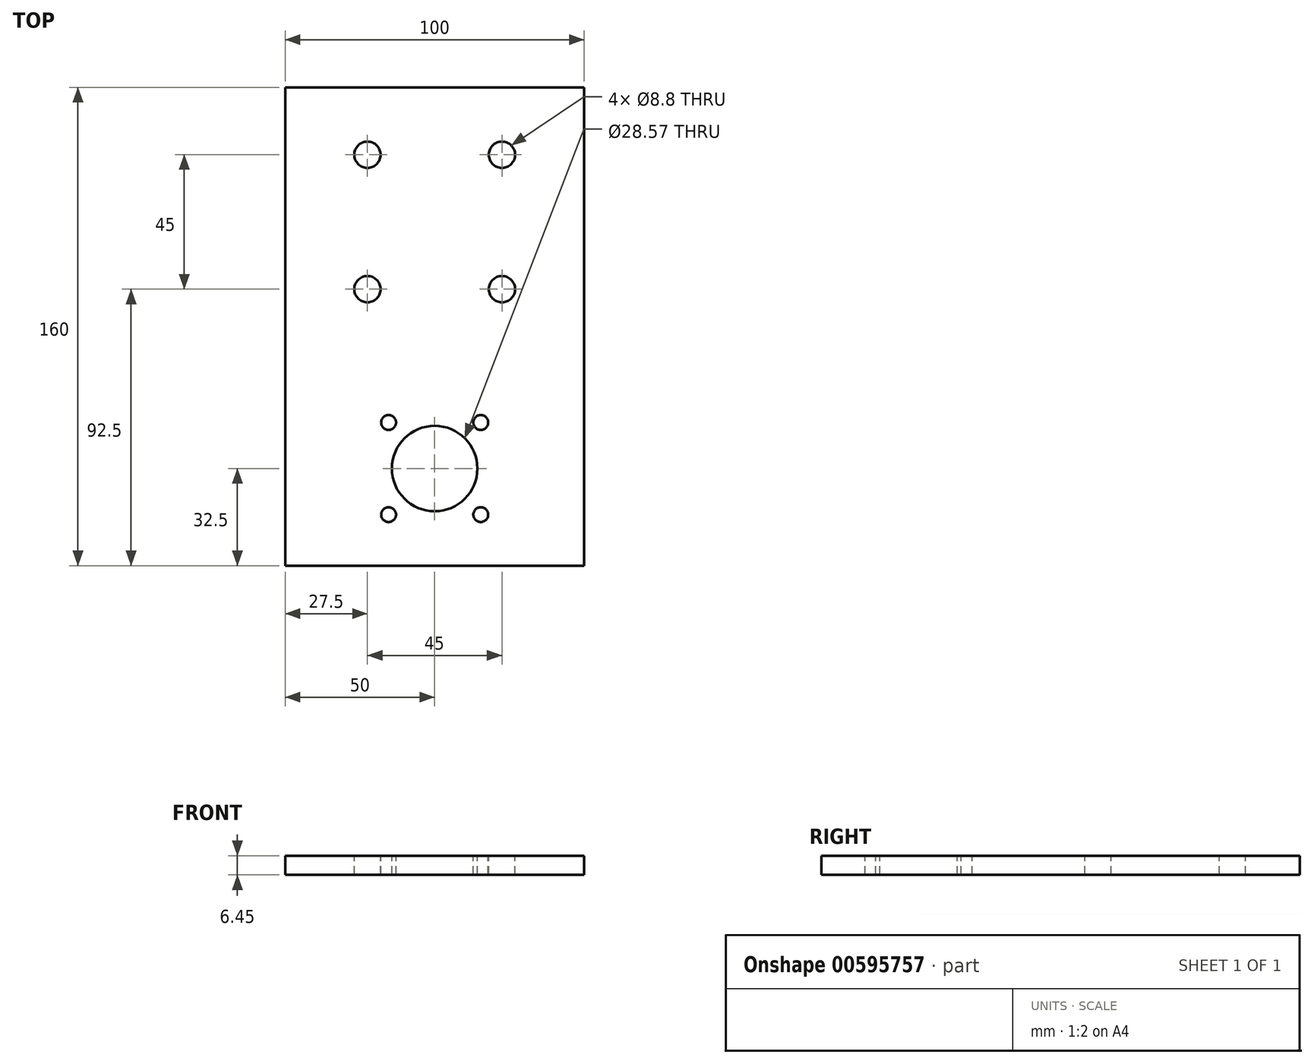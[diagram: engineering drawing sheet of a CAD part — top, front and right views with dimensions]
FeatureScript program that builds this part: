
annotation { "Feature Type Name" : "Feature", "Feature Type Description" : "" }
export const myFeature = defineFeature(function(context is Context, id is Id, definition is map)
    precondition{}
    {
        {
            var Q0;
            Q0=qCreatedBy(makeId("Top.planeOp"),FACE);
            var sketch = newSketch(context, id + "F0", { "sketchPlane" : qUnion([Q0])});
            skLineSegment(sketch, "E0.bottom", {"start": v(-50, 80) * mm, "end": v(50, 80) * mm});
            skLineSegment(sketch, "E0.top", {"start": v(-50, -80) * mm, "end": v(50, -80) * mm});
            skLineSegment(sketch, "E0.left", {"start": v(-50, 80) * mm, "end": v(-50, -80) * mm});
            skLineSegment(sketch, "E0.right", {"start": v(50, 80) * mm, "end": v(50, -80) * mm});
            skPoint(sketch, "E0.middle", {"position": v(0, 0) * mm});
            skSolve(sketch);
        }
        {
            var Q0;
            Q0=makeQuery(id+"F0.imprint","IMPRINT",FACE,{"disambiguationData":[TD([[makeQuery(id+"F0.imprint","IMPRINT",EDGE,{"derivedFrom":sQuery(id+"F0.wireOp",EDGE,"E0.bottom")}),-1.0]])]});
            extrude(context, id + "F1", {"entities" : qUnion([Q0]), "depth" : 6.45 * mm, "offsetDistance" : 25 * mm});
        }
        {
            var Q0;
            Q0=makeQuery(id+"F1.opExtrude","CAP_FACE",FACE,{"disambiguationData":[OSD([sQuery(id+"F0.wireOp",EDGE,"E0.bottom"),sQuery(id+"F0.wireOp",EDGE,"E0.top"),sQuery(id+"F0.wireOp",EDGE,"E0.left"),sQuery(id+"F0.wireOp",EDGE,"E0.right")])],"isStart":false});
            var sketch = newSketch(context, id + "F2", { "sketchPlane" : qUnion([Q0])});
            skLineSegment(sketch, "E1.bottom", {"start": v(-22.5, 12.5) * mm, "end": v(22.5, 12.5) * mm, "construction": true});
            skLineSegment(sketch, "E1.top", {"start": v(-22.5, 57.5) * mm, "end": v(22.5, 57.5) * mm, "construction": true});
            skLineSegment(sketch, "E1.left", {"start": v(-22.5, 12.5) * mm, "end": v(-22.5, 57.5) * mm, "construction": true});
            skLineSegment(sketch, "E1.right", {"start": v(22.5, 12.5) * mm, "end": v(22.5, 57.5) * mm, "construction": true});
            skPoint(sketch, "E1.middle", {"position": v(0, 35) * mm});
            skPoint(sketch, "E2", {"position": v(-22.5, 57.5) * mm});
            skPoint(sketch, "E3", {"position": v(22.5, 57.5) * mm});
            skPoint(sketch, "E4", {"position": v(22.5, 12.5) * mm});
            skPoint(sketch, "E5", {"position": v(-22.5, 12.5) * mm});
            skSolve(sketch);
        }
        {
            var Q0;
            Q0=sQuery(id+"F2.wireOp",VERTEX,"E2");
            var Q1;
            Q1=sQuery(id+"F2.wireOp",VERTEX,"E3");
            var Q2;
            Q2=sQuery(id+"F2.wireOp",VERTEX,"E4");
            var Q3;
            Q3=sQuery(id+"F2.wireOp",VERTEX,"E5");
            var Q4;
            Q4=makeQuery(id+"F1.opExtrude","SWEPT_BODY",BODY,{"disambiguationData":[OSD([sQuery(id+"F0.wireOp",EDGE,"E0.bottom"),sQuery(id+"F0.wireOp",EDGE,"E0.top"),sQuery(id+"F0.wireOp",EDGE,"E0.left"),sQuery(id+"F0.wireOp",EDGE,"E0.right")])]});
            hole(context, id + "F3", {"style" : HoleStyle.SIMPLE, "endStyle" : HoleEndStyle.THROUGH, "standardTappedOrClearance" : lookupTablePath({ "standard" : "ISO", "fit" : "Normal", "size" : "M8", "type" : "Clearance" }), "standardBlindInLast" : lookupTablePath({ "fit" : "Standard", "standard" : "ISO", "size" : "M8", "type" : "Clearance" }), "holeDiameter" : 8.8 * mm, "majorDiameter" : 5 * mm, "isTappedThrough" : true, "tappedDepth" : 12 * mm, "tapClearance" : 3, "locations" : qUnion([Q0, Q1, Q2, Q3]), "scope" : qUnion([Q4])});
        }
        {
            var Q0;
            Q0=makeQuery(id+"F1.opExtrude","CAP_FACE",FACE,{"disambiguationData":[OSD([sQuery(id+"F0.wireOp",EDGE,"E0.bottom"),sQuery(id+"F0.wireOp",EDGE,"E0.top"),sQuery(id+"F0.wireOp",EDGE,"E0.left"),sQuery(id+"F0.wireOp",EDGE,"E0.right")])],"isStart":false});
            var sketch = newSketch(context, id + "F4", { "sketchPlane" : qUnion([Q0])});
            skCircle(sketch, "E6", {"center": v(0, -47.5) * mm, "radius": 21.8 * mm, "construction": true});
            skCircle(sketch, "E7.0", {"center": v(22.5, 12.5) * mm, "radius": 4.4 * mm, "construction": true});
            skCircle(sketch, "E7.1", {"center": v(-22.5, 12.5) * mm, "radius": 4.4 * mm, "construction": true});
            skLineSegment(sketch, "E8", {"start": v(-15.41, -32.09) * mm, "end": v(15.41, -62.91) * mm, "construction": true});
            skLineSegment(sketch, "E9", {"start": v(-15.41, -62.91) * mm, "end": v(15.41, -32.09) * mm, "construction": true});
            skPoint(sketch, "E10", {"position": v(-15.41, -32.09) * mm});
            skPoint(sketch, "E11", {"position": v(15.41, -32.09) * mm});
            skPoint(sketch, "E12", {"position": v(-15.41, -62.91) * mm});
            skPoint(sketch, "E13", {"position": v(15.41, -62.91) * mm});
            skSolve(sketch);
        }
        {
            var Q0;
            Q0=sQuery(id+"F4.wireOp",VERTEX,"E10");
            var Q1;
            Q1=sQuery(id+"F4.wireOp",VERTEX,"E11");
            var Q2;
            Q2=sQuery(id+"F4.wireOp",VERTEX,"E13");
            var Q3;
            Q3=sQuery(id+"F4.wireOp",VERTEX,"E12");
            var Q4;
            Q4=makeQuery(id+"F1.opExtrude","SWEPT_BODY",BODY,{"disambiguationData":[OSD([sQuery(id+"F0.wireOp",EDGE,"E0.bottom"),sQuery(id+"F0.wireOp",EDGE,"E0.top"),sQuery(id+"F0.wireOp",EDGE,"E0.left"),sQuery(id+"F0.wireOp",EDGE,"E0.right")])]});
            hole(context, id + "F5", {"style" : HoleStyle.SIMPLE, "endStyle" : HoleEndStyle.THROUGH, "standardTappedOrClearance" : lookupTablePath({ "standard" : "ANSI", "fit" : "Close", "size" : "#10", "type" : "Clearance" }), "standardBlindInLast" : lookupTablePath({ "fit" : "Close", "standard" : "ANSI", "size" : "#10", "type" : "Clearance" }), "holeDiameter" : 4.98 * mm, "majorDiameter" : 5 * mm, "isTappedThrough" : true, "tappedDepth" : 12 * mm, "tapClearance" : 3, "locations" : qUnion([Q0, Q1, Q2, Q3]), "scope" : qUnion([Q4])});
        }
        {
            var Q0;
            Q0=makeQuery(id+"F1.opExtrude","CAP_FACE",FACE,{"disambiguationData":[OSD([sQuery(id+"F0.wireOp",EDGE,"E0.bottom"),sQuery(id+"F0.wireOp",EDGE,"E0.top"),sQuery(id+"F0.wireOp",EDGE,"E0.left"),sQuery(id+"F0.wireOp",EDGE,"E0.right")])],"isStart":false});
            var sketch = newSketch(context, id + "F6", { "sketchPlane" : qUnion([Q0])});
            skPoint(sketch, "E14", {"position": v(0, -47.5) * mm});
            skCircle(sketch, "E15.0", {"center": v(22.5, 12.5) * mm, "radius": 4.4 * mm, "construction": true});
            skSolve(sketch);
        }
        {
            var Q0;
            Q0=sQuery(id+"F6.wireOp",VERTEX,"E14");
            var Q1;
            Q1=makeQuery(id+"F1.opExtrude","SWEPT_BODY",BODY,{"disambiguationData":[OSD([sQuery(id+"F0.wireOp",EDGE,"E0.bottom"),sQuery(id+"F0.wireOp",EDGE,"E0.top"),sQuery(id+"F0.wireOp",EDGE,"E0.left"),sQuery(id+"F0.wireOp",EDGE,"E0.right")])]});
            hole(context, id + "F7", {"style" : HoleStyle.SIMPLE, "endStyle" : HoleEndStyle.THROUGH, "holeDiameter" : 28.57 * mm, "majorDiameter" : 5 * mm, "isTappedThrough" : true, "tappedDepth" : 12 * mm, "tapClearance" : 3, "locations" : qUnion([Q0]), "scope" : qUnion([Q1])});
        }
    });
